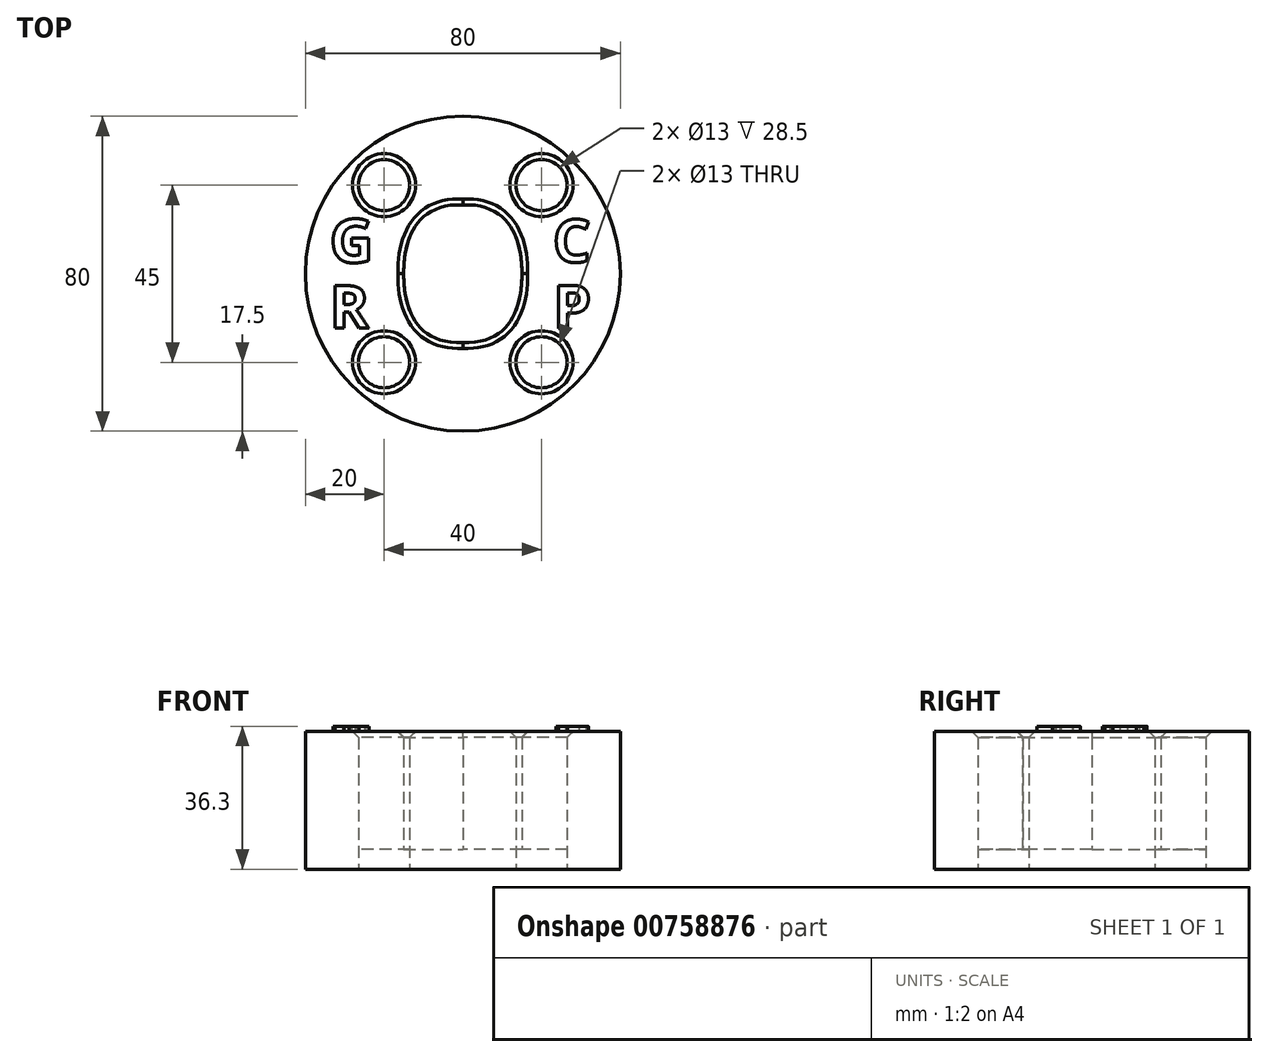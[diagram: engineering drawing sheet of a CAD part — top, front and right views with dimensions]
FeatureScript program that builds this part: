
annotation { "Feature Type Name" : "Feature", "Feature Type Description" : "" }
export const myFeature = defineFeature(function(context is Context, id is Id, definition is map)
    precondition{}
    {
        {
            var Q0;
            Q0=qCreatedBy(makeId("Top.planeOp"),FACE);
            var sketch = newSketch(context, id + "F0", { "sketchPlane" : qUnion([Q0])});
            skCircle(sketch, "E0", {"center": v(0, 0) * mm, "radius": 40 * mm});
            skLineSegment(sketch, "E1", {"start": v(0, 0) * mm, "end": v(0, 40) * mm, "construction": true});
            skLineSegment(sketch, "E2", {"start": v(0, 0) * mm, "end": v(40, 0) * mm, "construction": true});
            skLineSegment(sketch, "E3", {"start": v(0, 0) * mm, "end": v(0, -40) * mm, "construction": true});
            skLineSegment(sketch, "E4", {"start": v(0, 0) * mm, "end": v(-40, 0) * mm, "construction": true});
            skPoint(sketch, "E5.endSnap0", {"position": v(20, 0) * mm});
            skCircle(sketch, "E6", {"center": v(20, 22.5) * mm, "radius": 6.5 * mm});
            skLineSegment(sketch, "E7", {"start": v(0, 0) * mm, "end": v(15, 0) * mm});
            skFitSpline(sketch, "E8", {"points": [v(15, 0) * mm, v(0, 17.5) * mm], "startDerivative": vector(0.3, 21.12) * mm, "endDerivative": vector(-38.64, -1.5) * mm});
            skCircle(sketch, "E9.MirrorC", {"center": v(-20, 22.5) * mm, "radius": 6.5 * mm});
            skFitSpline(sketch, "E10.MirrorCS", {"points": [v(-15, 0) * mm, v(0, 17.5) * mm], "startDerivative": vector(-0.3, 21.12) * mm, "endDerivative": vector(38.64, -1.5) * mm});
            skFitSpline(sketch, "E11.MirrorCS", {"points": [v(-15, 0) * mm, v(0, -17.5) * mm], "startDerivative": vector(-0.3, -21.12) * mm, "endDerivative": vector(38.64, 1.5) * mm});
            skCircle(sketch, "E12.MirrorC", {"center": v(-20, -22.5) * mm, "radius": 6.5 * mm});
            skCircle(sketch, "E13.MirrorC", {"center": v(20, -22.5) * mm, "radius": 6.5 * mm});
            skFitSpline(sketch, "E14.MirrorCS", {"points": [v(15, 0) * mm, v(0, -17.5) * mm], "startDerivative": vector(0.3, -21.12) * mm, "endDerivative": vector(-38.64, 1.5) * mm});
            skLineSegment(sketch, "E15.bottom", {"start": v(-22.93, 2.86) * mm, "end": v(-33.93, 2.94) * mm, "construction": true});
            skLineSegment(sketch, "E15.top", {"start": v(-22.85, 13.85) * mm, "end": v(-33.85, 13.94) * mm, "construction": true});
            skLineSegment(sketch, "E15.left", {"start": v(-22.93, 2.86) * mm, "end": v(-22.85, 13.85) * mm, "construction": true});
            skLineSegment(sketch, "E15.right", {"start": v(-33.93, 2.94) * mm, "end": v(-33.85, 13.94) * mm, "construction": true});
            skPoint(sketch, "E15.middle", {"position": v(-28.4, 8.4) * mm});
            skLineSegment(sketch, "E16.MirrorCS", {"start": v(22.93, 2.86) * mm, "end": v(22.85, 13.85) * mm, "construction": true});
            skLineSegment(sketch, "E17.MirrorCS", {"start": v(22.85, 13.85) * mm, "end": v(33.85, 13.94) * mm, "construction": true});
            skLineSegment(sketch, "E18.MirrorCS", {"start": v(33.93, 2.94) * mm, "end": v(33.85, 13.94) * mm, "construction": true});
            skLineSegment(sketch, "E19.MirrorCS", {"start": v(22.93, 2.86) * mm, "end": v(33.93, 2.94) * mm, "construction": true});
            skLineSegment(sketch, "E20.MirrorCS", {"start": v(-22.93, -2.86) * mm, "end": v(-33.93, -2.94) * mm, "construction": true});
            skLineSegment(sketch, "E21.MirrorCS", {"start": v(-22.93, -2.86) * mm, "end": v(-22.85, -13.85) * mm, "construction": true});
            skLineSegment(sketch, "E22.MirrorCS", {"start": v(-22.85, -13.85) * mm, "end": v(-33.85, -13.94) * mm, "construction": true});
            skLineSegment(sketch, "E23.MirrorCS", {"start": v(-33.93, -2.94) * mm, "end": v(-33.85, -13.94) * mm, "construction": true});
            skLineSegment(sketch, "E24.MirrorCS", {"start": v(22.93, -2.86) * mm, "end": v(22.85, -13.85) * mm, "construction": true});
            skLineSegment(sketch, "E25.MirrorCS", {"start": v(22.93, -2.86) * mm, "end": v(33.93, -2.94) * mm, "construction": true});
            skLineSegment(sketch, "E26.MirrorCS", {"start": v(33.93, -2.94) * mm, "end": v(33.85, -13.94) * mm, "construction": true});
            skLineSegment(sketch, "E27.MirrorCS", {"start": v(22.85, -13.85) * mm, "end": v(33.85, -13.94) * mm, "construction": true});
            skText(sketch, "E28", { "text": "G", "fontName": "OpenSans-Bold.ttf"});
            skText(sketch, "E29", { "text": "R", "fontName": "OpenSans-Bold.ttf"});
            skText(sketch, "E30", { "text": "C", "fontName": "OpenSans-Bold.ttf"});
            skText(sketch, "E31", { "text": "P", "fontName": "OpenSans-Bold.ttf"});
            const initialGuessF0  = {"E28": [-0.03385, 0.00286, 1, 0, 0.01109], "E29": [-0.03384, -0.01385, 1, 0, 0.01091], "E30": [0.02285, 0.00294, 1, 0, 0.01091], "E31": [0.02293, -0.01394, 1, 0, 0.01109]};
            skSetInitialGuess(sketch, initialGuessF0);
            skSolve(sketch);
        }
        {
            var Q0;
            Q0 = qSketchRegion(id + "F0", true);
            extrude(context, id + "F1", {"entities" : qUnion([Q0]), "depth" : 35 * mm, "offsetDistance" : 25 * mm});
        }
        {
            var Q0;
            Q0=makeQuery(id+"F0.imprint","IMPRINT",FACE,{"disambiguationData":[TD([[makeQuery(id+"F0.imprint","IMPRINT",EDGE,{"derivedFrom":sQuery(id+"F0.wireOp",EDGE,"E31.sketch_text.stroke-0")}),-1.0]])]});
            var Q1;
            Q1=makeQuery(id+"F0.imprint","IMPRINT",FACE,{"disambiguationData":[TD([[makeQuery(id+"F0.imprint","IMPRINT",EDGE,{"derivedFrom":sQuery(id+"F0.wireOp",EDGE,"E30.sketch_text.stroke-0")}),-1.0]])]});
            var Q2;
            Q2=makeQuery(id+"F0.imprint","IMPRINT",FACE,{"disambiguationData":[TD([[makeQuery(id+"F0.imprint","IMPRINT",EDGE,{"derivedFrom":sQuery(id+"F0.wireOp",EDGE,"E28.sketch_text.stroke-0")}),-1.0]])]});
            var Q3;
            Q3=makeQuery(id+"F0.imprint","IMPRINT",FACE,{"disambiguationData":[TD([[makeQuery(id+"F0.imprint","IMPRINT",EDGE,{"derivedFrom":sQuery(id+"F0.wireOp",EDGE,"E29.sketch_text.stroke-0")}),-1.0]])]});
            extrude(context, id + "F2", {"entities" : qUnion([Q0, Q1, Q2, Q3]), "operationType" : NewBodyOperationType.ADD, "depth" : 36.3 * mm, "offsetDistance" : 25 * mm});
        }
        {
            var Q0;
            Q0=makeQuery(id+"F0.imprint","IMPRINT",FACE,{"disambiguationData":[TD([[makeQuery(id+"F0.imprint","IMPRINT",EDGE,{"derivedFrom":sQuery(id+"F0.wireOp",EDGE,"E31.sketch_text.stroke-0")}),1.0]])]});
            var Q1;
            Q1=makeQuery(id+"F0.imprint","IMPRINT",FACE,{"disambiguationData":[TD([[makeQuery(id+"F0.imprint","IMPRINT",EDGE,{"derivedFrom":sQuery(id+"F0.wireOp",EDGE,"E29.sketch_text.stroke-0")}),1.0]])]});
            extrude(context, id + "F3", {"entities" : qUnion([Q0, Q1]), "operationType" : NewBodyOperationType.ADD, "depth" : 35 * mm, "offsetDistance" : 25 * mm});
        }
        {
            var Q0;
            Q0=makeQuery(id+"F0.imprint","IMPRINT",FACE,{"disambiguationData":[TD([[makeQuery(id+"F0.imprint","IMPRINT",EDGE,{"derivedFrom":sQuery(id+"F0.wireOp",EDGE,"E9.MirrorC")}),-1.0]])]});
            var Q1;
            Q1=makeQuery(id+"F0.imprint","IMPRINT",FACE,{"disambiguationData":[TD([[makeQuery(id+"F0.imprint","IMPRINT",EDGE,{"derivedFrom":sQuery(id+"F0.wireOp",EDGE,"E6")}),1.0]])]});
            var Q2;
            Q2=makeQuery(id+"F0.imprint","IMPRINT",FACE,{"disambiguationData":[TD([[makeQuery(id+"F0.imprint","IMPRINT",EDGE,{"derivedFrom":sQuery(id+"F0.wireOp",EDGE,"E8")}),1.0]])]});
            var Q3;
            Q3=makeQuery(id+"F0.imprint","IMPRINT",FACE,{"disambiguationData":[TD([[makeQuery(id+"F0.imprint","IMPRINT",EDGE,{"derivedFrom":sQuery(id+"F0.wireOp",EDGE,"E13.MirrorC")}),-1.0]])]});
            var Q4;
            Q4=makeQuery(id+"F0.imprint","IMPRINT",FACE,{"disambiguationData":[TD([[makeQuery(id+"F0.imprint","IMPRINT",EDGE,{"derivedFrom":sQuery(id+"F0.wireOp",EDGE,"E12.MirrorC")}),1.0]])]});
            extrude(context, id + "F4", {"entities" : qUnion([Q0, Q1, Q2, Q3, Q4]), "operationType" : NewBodyOperationType.ADD, "depth" : 5 * mm, "offsetDistance" : 25 * mm});
        }
        {
            var Q0;
            Q0=makeQuery(id+"F1.opExtrude","CAP_EDGE",EDGE,{"disambiguationData":[OSD([sQuery(id+"F0.wireOp",EDGE,"E10.MirrorCS")])],"isStart":false});
            var Q1;
            Q1=makeQuery(id+"F1.opExtrude","CAP_EDGE",EDGE,{"disambiguationData":[OSD([sQuery(id+"F0.wireOp",EDGE,"E8")])],"isStart":false});
            var Q2;
            Q2=makeQuery(id+"F1.opExtrude","CAP_EDGE",EDGE,{"disambiguationData":[OSD([sQuery(id+"F0.wireOp",EDGE,"E14.MirrorCS")])],"isStart":false});
            var Q3;
            Q3=makeQuery(id+"F1.opExtrude","CAP_EDGE",EDGE,{"disambiguationData":[OSD([sQuery(id+"F0.wireOp",EDGE,"E11.MirrorCS")])],"isStart":false});
            var Q4;
            Q4=makeQuery(id+"F1.opExtrude","CAP_EDGE",EDGE,{"disambiguationData":[OSD([sQuery(id+"F0.wireOp",EDGE,"E12.MirrorC")])],"isStart":false});
            var Q5;
            Q5=makeQuery(id+"F1.opExtrude","CAP_EDGE",EDGE,{"disambiguationData":[OSD([sQuery(id+"F0.wireOp",EDGE,"E9.MirrorC")])],"isStart":false});
            var Q6;
            Q6=makeQuery(id+"F1.opExtrude","CAP_EDGE",EDGE,{"disambiguationData":[OSD([sQuery(id+"F0.wireOp",EDGE,"E6")])],"isStart":false});
            var Q7;
            Q7=makeQuery(id+"F1.opExtrude","CAP_EDGE",EDGE,{"disambiguationData":[OSD([sQuery(id+"F0.wireOp",EDGE,"E13.MirrorC")])],"isStart":false});
            chamfer(context, id + "F5", {"entities" : qUnion([Q0, Q1, Q2, Q3, Q4, Q5, Q6, Q7]), "width" : 1.5 * mm, "tangentPropagation" : true});
        }
    });
